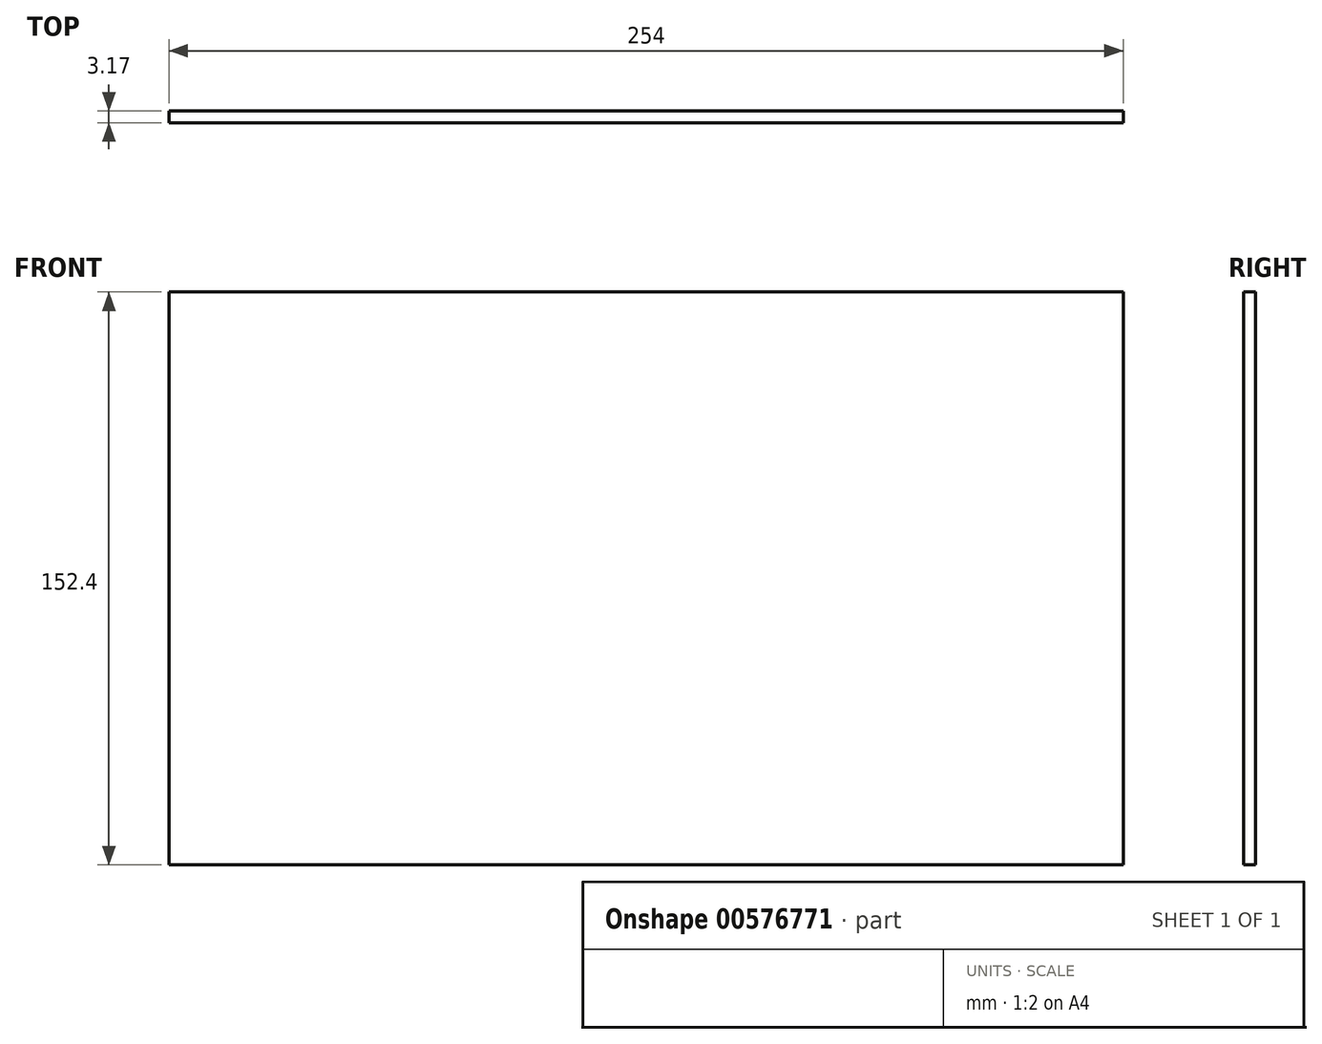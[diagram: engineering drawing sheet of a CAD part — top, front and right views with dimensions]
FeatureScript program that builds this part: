
annotation { "Feature Type Name" : "Feature", "Feature Type Description" : "" }
export const myFeature = defineFeature(function(context is Context, id is Id, definition is map)
    precondition{}
    {
        {
            var Q0;
            Q0=qCreatedBy(makeId("Front.planeOp"),FACE);
            var sketch = newSketch(context, id + "F0", { "sketchPlane" : qUnion([Q0])});
            skLineSegment(sketch, "E0.bottom", {"start": v(-152.06, 87.38) * mm, "end": v(101.94, 87.38) * mm});
            skLineSegment(sketch, "E0.top", {"start": v(-152.06, -65.02) * mm, "end": v(101.94, -65.02) * mm});
            skLineSegment(sketch, "E0.left", {"start": v(-152.06, 87.38) * mm, "end": v(-152.06, -65.02) * mm});
            skLineSegment(sketch, "E0.right", {"start": v(101.94, 87.38) * mm, "end": v(101.94, -65.02) * mm});
            skSolve(sketch);
        }
        {
            var Q0;
            Q0 = qSketchRegion(id + "F0", true);
            extrude(context, id + "F1", {"entities" : qUnion([Q0]), "depth" : 3.17 * mm, "offsetDistance" : 25.4 * mm});
        }
    });
